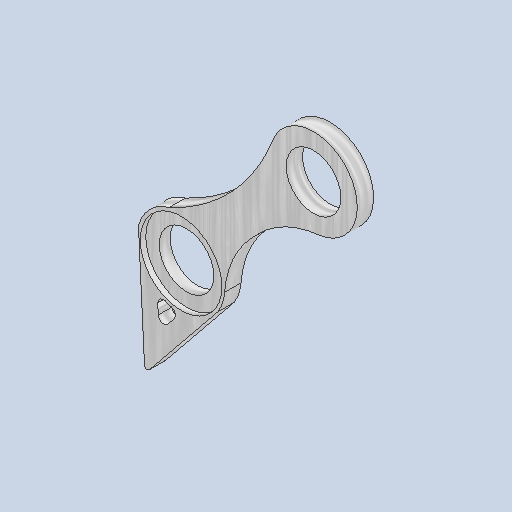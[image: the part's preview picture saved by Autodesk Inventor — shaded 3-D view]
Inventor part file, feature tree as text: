
AUTODESK INVENTOR PART (.ipt)
format: ipt  version: 2023 (Build 270158030, 158C)  size: 378,368 bytes
history: native  units: mm
features: sketch x12, extrude x10, fillet x6, other x5, projected_geometry x4
ambient origin geometry x8: Origin, YZ Plane, XZ Plane, XY Plane, X Axis, Y Axis, Z Axis, Center Point
bodies: Body1 (feature_tree)
feature tree (37):
  extrude  "押し出し2"  TaperAngle=45.0deg  [1 undecoded]
  fillet  "フィレット2"  Radius=3.0mm
  extrude  "押し出し3"  Depth=0.5mm
  fillet  "フィレット3"  Radius=0.5mm
  sketch  "スケッチ4"
  sketch  "スケッチ5"
  extrude  "押し出し4"  TaperAngle=0.0deg  [1 undecoded]
  extrude  "押し出し5"  Depth=1.0mm
  extrude  "押し出し6"  Depth=1.0mm
  sketch  "スケッチ6"
  sketch  "スケッチ7"
  extrude  "押し出し7"  Depth=3.0mm TaperAngle=0.0deg
  fillet  "フィレット4"  Radius=3.0mm
  extrude  "押し出し8"  Depth=3.0mm TaperAngle=0.0deg
  fillet  "フィレット5"  Radius=4.5mm
  sketch  "スケッチ10"
  extrude  "押し出し9"  Depth=4.0mm
  fillet  "フィレット6"  Radius=10.0mm
  extrude  "押し出し10"  Depth=18.0mm
  fillet  "フィレット7"  Radius=3.0mm
  extrude  "押し出し11"  Depth=2.5mm TaperAngle=0.0deg
  sketch  "スケッチ2"
  sketch  "スケッチ3"
  sketch  "スケッチ8"
  sketch  "スケッチ9"
  projected_geometry  "投影ループ1"
  sketch  "スケッチ11"
  projected_geometry  "投影ループ2"
  sketch  "スケッチ12"
  projected_geometry  "投影ループ3"
  sketch  "スケッチ13"
  projected_geometry  "投影ループ4"
  other  "断面エッジを投影1"
  other  "断面エッジを投影2"
  other  "断面エッジを投影3"
  other  "断面エッジを投影4"
  other  "断面エッジを投影5"
note: 2 required parameter values undecoded (feature->parameter linkage not recoverable at this tier; creation-order binding heuristic only, values carry confidence <= 0.55)
